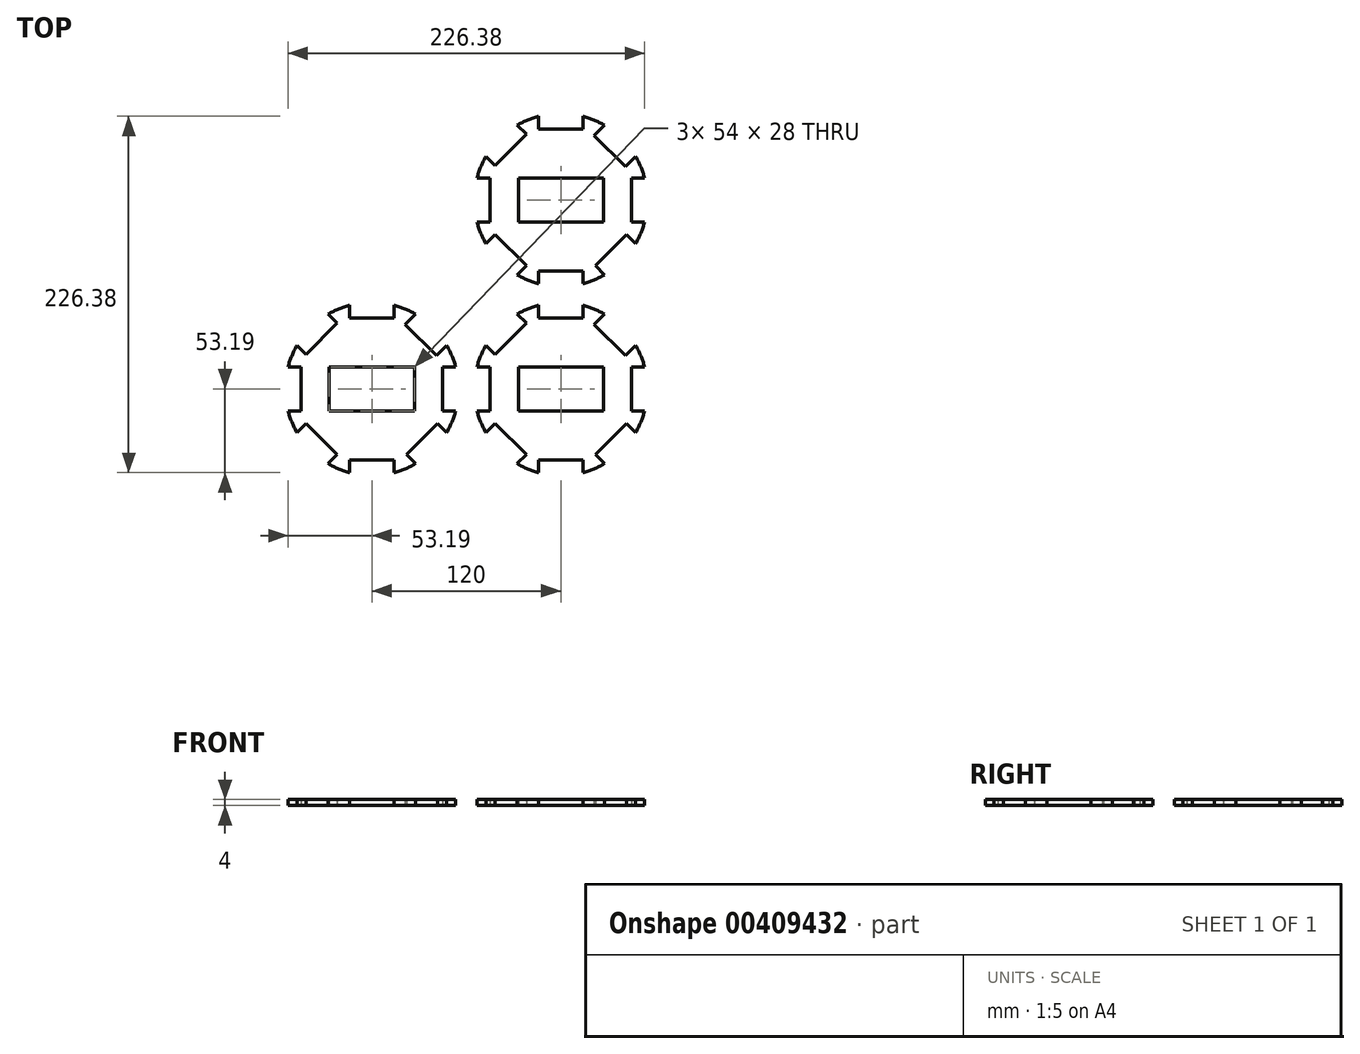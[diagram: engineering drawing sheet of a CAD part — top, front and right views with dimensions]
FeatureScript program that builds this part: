
annotation { "Feature Type Name" : "Feature", "Feature Type Description" : "" }
export const myFeature = defineFeature(function(context is Context, id is Id, definition is map)
    precondition{}
    {
        {
            var Q0;
            Q0=qCreatedBy(makeId("Top.planeOp"),FACE);
            var sketch = newSketch(context, id + "F0", { "sketchPlane" : qUnion([Q0])});
            skArc(sketch, "E0", {"start": v(14, -53.19) * mm, "mid": v(21.05, -50.81) * mm, "end": v(27.71, -47.5) * mm});
            skLineSegment(sketch, "E1.bottom", {"start": v(27, 14) * mm, "end": v(-27, 14) * mm});
            skLineSegment(sketch, "E1.top", {"start": v(27, -14) * mm, "end": v(-27, -14) * mm});
            skLineSegment(sketch, "E1.left", {"start": v(27, 14) * mm, "end": v(27, -14) * mm});
            skLineSegment(sketch, "E1.right", {"start": v(-27, 14) * mm, "end": v(-27, -14) * mm});
            skLineSegment(sketch, "E2", {"start": v(0, 66.65) * mm, "end": v(0, -85.59) * mm, "construction": true});
            skLineSegment(sketch, "E3", {"start": v(67.17, 0) * mm, "end": v(-84.57, 0) * mm, "construction": true});
            skLineSegment(sketch, "E4", {"start": v(-14, 45) * mm, "end": v(14, 45) * mm});
            skLineSegment(sketch, "E5", {"start": v(86.43, -45) * mm, "end": v(86.43, -46.57) * mm});
            skLineSegment(sketch, "E6", {"start": v(-14, 53.19) * mm, "end": v(-14, 45) * mm});
            skLineSegment(sketch, "E7", {"start": v(14, 53.19) * mm, "end": v(14, 45) * mm});
            skLineSegment(sketch, "E8", {"start": v(-14, -45) * mm, "end": v(-14, -53.19) * mm});
            skPoint(sketch, "E8.startSnap0", {"position": v(-14, 49.1) * mm});
            skLineSegment(sketch, "E9", {"start": v(14, -45) * mm, "end": v(14, -53.19) * mm});
            skPoint(sketch, "E10.orphan", {"position": v(-14, -34.53) * mm});
            skPoint(sketch, "E11.orphan", {"position": v(14, -36.88) * mm});
            skArc(sketch, "E12.trimOffspring", {"start": v(-14, 53.19) * mm, "mid": v(-21.05, 50.81) * mm, "end": v(-27.71, 47.5) * mm});
            skLineSegment(sketch, "E13", {"start": v(45, 14) * mm, "end": v(53.19, 14) * mm});
            skLineSegment(sketch, "E14", {"start": v(45, -14) * mm, "end": v(53.19, -14) * mm});
            skLineSegment(sketch, "E15", {"start": v(45, 14) * mm, "end": v(45, -14) * mm});
            skPoint(sketch, "E16.orphan", {"position": v(81, 14) * mm});
            skPoint(sketch, "E17.orphan", {"position": v(81, -14) * mm});
            skPoint(sketch, "E18.orphan", {"position": v(40.73, -14) * mm});
            skPoint(sketch, "E19.orphan", {"position": v(40.73, 14) * mm});
            skArc(sketch, "E20.trimOffspring", {"start": v(53.19, 14) * mm, "mid": v(50.81, 21.05) * mm, "end": v(47.5, 27.71) * mm});
            skLineSegment(sketch, "E21", {"start": v(-45, 14) * mm, "end": v(-53.19, 14) * mm});
            skLineSegment(sketch, "E22", {"start": v(-45, -14) * mm, "end": v(-53.19, -14) * mm});
            skLineSegment(sketch, "E23", {"start": v(-45, 14) * mm, "end": v(-45, -14) * mm});
            skPoint(sketch, "E24.orphan", {"position": v(-45, 14) * mm});
            skPoint(sketch, "E25.orphan", {"position": v(-41.1, -14) * mm});
            skArc(sketch, "E26.trimOffspring", {"start": v(-53.19, -14) * mm, "mid": v(-50.81, -21.05) * mm, "end": v(-47.5, -27.71) * mm});
            skPoint(sketch, "E27.orphan", {"position": v(-70.98, 14) * mm});
            skPoint(sketch, "E28.orphan", {"position": v(-70.98, -14) * mm});
            skLineSegment(sketch, "E29", {"start": v(-47.6, 48.89) * mm, "end": v(0, 0) * mm, "construction": true});
            skLineSegment(sketch, "E30.0", {"start": v(-41.72, -21.92) * mm, "end": v(-21.92, -41.72) * mm});
            skLineSegment(sketch, "E31", {"start": v(0, 0) * mm, "end": v(49.98, -49.98) * mm, "construction": true});
            skLineSegment(sketch, "E32", {"start": v(0, 0) * mm, "end": v(50.7, 50.7) * mm, "construction": true});
            skLineSegment(sketch, "E33", {"start": v(0, 0) * mm, "end": v(-45.25, -45.25) * mm, "construction": true});
            skLineSegment(sketch, "E34.0", {"start": v(-47.5, -27.71) * mm, "end": v(-41.72, -21.92) * mm});
            skLineSegment(sketch, "E35.0", {"start": v(-27.71, -47.5) * mm, "end": v(-21.92, -41.72) * mm});
            skLineSegment(sketch, "E36.trimOffspring", {"start": v(21.22, 41.02) * mm, "end": v(41.02, 21.22) * mm});
            skArc(sketch, "E37.trimOffspring", {"start": v(27.71, 47.5) * mm, "mid": v(21.05, 50.81) * mm, "end": v(14, 53.19) * mm});
            skArc(sketch, "E38.trimOffspring", {"start": v(-27.71, -47.5) * mm, "mid": v(-21.05, -50.81) * mm, "end": v(-14, -53.19) * mm});
            skLineSegment(sketch, "E39.trimOffspring", {"start": v(-14, -45) * mm, "end": v(14, -45) * mm});
            skLineSegment(sketch, "E40.trimOffspring", {"start": v(21.22, 41.02) * mm, "end": v(27.71, 47.5) * mm});
            skLineSegment(sketch, "E41.trimOffspring", {"start": v(41.02, 21.22) * mm, "end": v(47.5, 27.71) * mm});
            skLineSegment(sketch, "E42.0", {"start": v(21.92, -41.72) * mm, "end": v(41.72, -21.92) * mm});
            skLineSegment(sketch, "E43.0", {"start": v(-27.71, 47.5) * mm, "end": v(-21.92, 41.72) * mm});
            skLineSegment(sketch, "E44.0", {"start": v(-47.5, 27.71) * mm, "end": v(-41.72, 21.92) * mm});
            skArc(sketch, "E45.trimOffspring", {"start": v(47.5, -27.71) * mm, "mid": v(50.81, -21.05) * mm, "end": v(53.19, -14) * mm});
            skLineSegment(sketch, "E46.0", {"start": v(-41.72, 21.92) * mm, "end": v(-21.92, 41.72) * mm});
            skArc(sketch, "E47.trimOffspring", {"start": v(-47.5, 27.71) * mm, "mid": v(-50.81, 21.05) * mm, "end": v(-53.19, 14) * mm});
            skLineSegment(sketch, "E48.trimOffspring", {"start": v(21.92, -41.72) * mm, "end": v(27.71, -47.5) * mm});
            skLineSegment(sketch, "E49.trimOffspring", {"start": v(41.72, -21.92) * mm, "end": v(47.5, -27.71) * mm});
            skSolve(sketch);
        }
        {
            var Q0;
            Q0 = qSketchRegion(id + "F0", true);
            extrude(context, id + "F1", {"entities" : qUnion([Q0]), "depth" : 4 * mm, "offsetDistance" : 25 * mm});
        }
        {
            var Q0;
            Q0=makeQuery(id+"F1.opExtrude","SWEPT_BODY",BODY,{"disambiguationData":[OSD([sQuery(id+"F0.wireOp",EDGE,"E0"),sQuery(id+"F0.wireOp",EDGE,"E1.bottom"),sQuery(id+"F0.wireOp",EDGE,"E1.top"),sQuery(id+"F0.wireOp",EDGE,"E1.left"),sQuery(id+"F0.wireOp",EDGE,"E1.right"),sQuery(id+"F0.wireOp",EDGE,"E4"),sQuery(id+"F0.wireOp",EDGE,"E6"),sQuery(id+"F0.wireOp",EDGE,"E7"),sQuery(id+"F0.wireOp",EDGE,"E8"),sQuery(id+"F0.wireOp",EDGE,"E9"),sQuery(id+"F0.wireOp",EDGE,"E12.trimOffspring"),sQuery(id+"F0.wireOp",EDGE,"E13"),sQuery(id+"F0.wireOp",EDGE,"E14"),sQuery(id+"F0.wireOp",EDGE,"E15"),sQuery(id+"F0.wireOp",EDGE,"E20.trimOffspring"),sQuery(id+"F0.wireOp",EDGE,"E21"),sQuery(id+"F0.wireOp",EDGE,"E22"),sQuery(id+"F0.wireOp",EDGE,"E23"),sQuery(id+"F0.wireOp",EDGE,"E26.trimOffspring"),sQuery(id+"F0.wireOp",EDGE,"E30.0"),sQuery(id+"F0.wireOp",EDGE,"E34.0"),sQuery(id+"F0.wireOp",EDGE,"E35.0"),sQuery(id+"F0.wireOp",EDGE,"E36.trimOffspring"),sQuery(id+"F0.wireOp",EDGE,"E37.trimOffspring"),sQuery(id+"F0.wireOp",EDGE,"E38.trimOffspring"),sQuery(id+"F0.wireOp",EDGE,"E39.trimOffspring"),sQuery(id+"F0.wireOp",EDGE,"E40.trimOffspring"),sQuery(id+"F0.wireOp",EDGE,"E41.trimOffspring"),sQuery(id+"F0.wireOp",EDGE,"E42.0"),sQuery(id+"F0.wireOp",EDGE,"E43.0"),sQuery(id+"F0.wireOp",EDGE,"E44.0"),sQuery(id+"F0.wireOp",EDGE,"E45.trimOffspring"),sQuery(id+"F0.wireOp",EDGE,"E46.0"),sQuery(id+"F0.wireOp",EDGE,"E47.trimOffspring"),sQuery(id+"F0.wireOp",EDGE,"E48.trimOffspring"),sQuery(id+"F0.wireOp",EDGE,"E49.trimOffspring")])]});
            transform(context, id + "F2", {"entities" : qUnion([Q0]), "transformType" : TransformType.TRANSLATION_3D, "dx" : 120 * mm, "dy" : 0 * mm, "dz" : 0 * mm, "makeCopy" : true});
        }
        {
            var Q0;
            Q0=makeQuery(id+"F2.opPattern","COPY",BODY,{"derivedFrom":makeQuery(id+"F1.opExtrude","SWEPT_BODY",BODY,{"disambiguationData":[OSD([sQuery(id+"F0.wireOp",EDGE,"E0"),sQuery(id+"F0.wireOp",EDGE,"E1.bottom"),sQuery(id+"F0.wireOp",EDGE,"E1.top"),sQuery(id+"F0.wireOp",EDGE,"E1.left"),sQuery(id+"F0.wireOp",EDGE,"E1.right"),sQuery(id+"F0.wireOp",EDGE,"E4"),sQuery(id+"F0.wireOp",EDGE,"E6"),sQuery(id+"F0.wireOp",EDGE,"E7"),sQuery(id+"F0.wireOp",EDGE,"E8"),sQuery(id+"F0.wireOp",EDGE,"E9"),sQuery(id+"F0.wireOp",EDGE,"E12.trimOffspring"),sQuery(id+"F0.wireOp",EDGE,"E13"),sQuery(id+"F0.wireOp",EDGE,"E14"),sQuery(id+"F0.wireOp",EDGE,"E15"),sQuery(id+"F0.wireOp",EDGE,"E20.trimOffspring"),sQuery(id+"F0.wireOp",EDGE,"E21"),sQuery(id+"F0.wireOp",EDGE,"E22"),sQuery(id+"F0.wireOp",EDGE,"E23"),sQuery(id+"F0.wireOp",EDGE,"E26.trimOffspring"),sQuery(id+"F0.wireOp",EDGE,"E30.0"),sQuery(id+"F0.wireOp",EDGE,"E34.0"),sQuery(id+"F0.wireOp",EDGE,"E35.0"),sQuery(id+"F0.wireOp",EDGE,"E36.trimOffspring"),sQuery(id+"F0.wireOp",EDGE,"E37.trimOffspring"),sQuery(id+"F0.wireOp",EDGE,"E38.trimOffspring"),sQuery(id+"F0.wireOp",EDGE,"E39.trimOffspring"),sQuery(id+"F0.wireOp",EDGE,"E40.trimOffspring"),sQuery(id+"F0.wireOp",EDGE,"E41.trimOffspring"),sQuery(id+"F0.wireOp",EDGE,"E42.0"),sQuery(id+"F0.wireOp",EDGE,"E43.0"),sQuery(id+"F0.wireOp",EDGE,"E44.0"),sQuery(id+"F0.wireOp",EDGE,"E45.trimOffspring"),sQuery(id+"F0.wireOp",EDGE,"E46.0"),sQuery(id+"F0.wireOp",EDGE,"E47.trimOffspring"),sQuery(id+"F0.wireOp",EDGE,"E48.trimOffspring"),sQuery(id+"F0.wireOp",EDGE,"E49.trimOffspring")])]}),"instanceName":"1"});
            transform(context, id + "F5", {"entities" : qUnion([Q0]), "transformType" : TransformType.TRANSLATION_3D, "dx" : 0 * mm, "dy" : 120 * mm, "dz" : 0 * mm, "makeCopy" : true});
        }
    });
